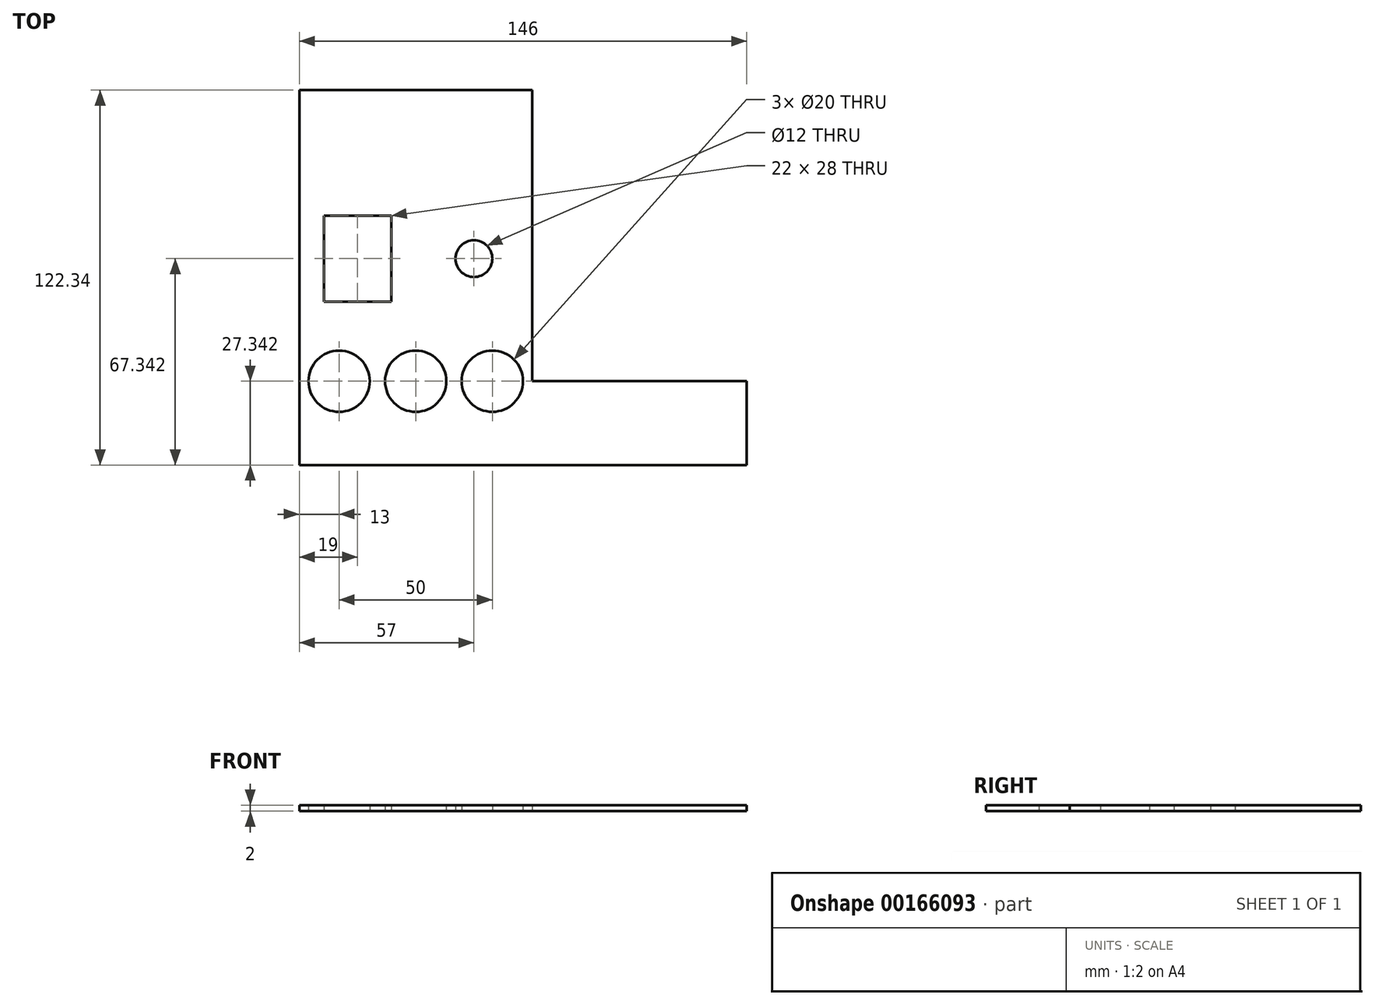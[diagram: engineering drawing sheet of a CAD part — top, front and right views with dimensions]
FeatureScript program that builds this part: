
annotation { "Feature Type Name" : "Feature", "Feature Type Description" : "" }
export const myFeature = defineFeature(function(context is Context, id is Id, definition is map)
    precondition{}
    {
        {
            var Q0;
            Q0=qCreatedBy(makeId("Top.planeOp"),FACE);
            var sketch = newSketch(context, id + "F0", { "sketchPlane" : qUnion([Q0])});
            skLineSegment(sketch, "E0.0", {"start": v(146, 0) * mm, "end": v(0, 0) * mm});
            skLineSegment(sketch, "E0.1", {"start": v(76, 122.34) * mm, "end": v(38, 122.34) * mm});
            skLineSegment(sketch, "E0.2", {"start": v(76, 122.34) * mm, "end": v(76, 27.34) * mm});
            skLineSegment(sketch, "E0.3", {"start": v(0, 0) * mm, "end": v(0, 122.34) * mm});
            skLineSegment(sketch, "E0.4", {"start": v(76, 27.34) * mm, "end": v(146, 27.34) * mm});
            skLineSegment(sketch, "E0.5", {"start": v(146, 0) * mm, "end": v(146, 27.34) * mm});
            skLineSegment(sketch, "E1", {"start": v(76, 27.34) * mm, "end": v(0, 27.34) * mm, "construction": true});
            skLineSegment(sketch, "E2", {"start": v(13, 46.21) * mm, "end": v(13, -10) * mm, "construction": true});
            skLineSegment(sketch, "E3", {"start": v(63, 46.64) * mm, "end": v(63, -8.92) * mm, "construction": true});
            skCircle(sketch, "E4", {"center": v(13, 27.34) * mm, "radius": 10 * mm});
            skCircle(sketch, "E5", {"center": v(38, 27.34) * mm, "radius": 10 * mm});
            skCircle(sketch, "E6", {"center": v(63, 27.34) * mm, "radius": 10 * mm});
            skLineSegment(sketch, "E7", {"start": v(38, 122.34) * mm, "end": v(38, -5.17) * mm, "construction": true});
            skLineSegment(sketch, "E8", {"start": v(38, 122.34) * mm, "end": v(0, 122.34) * mm});
            skLineSegment(sketch, "E9", {"start": v(93.77, 67.34) * mm, "end": v(-26.66, 67.34) * mm, "construction": true});
            skLineSegment(sketch, "E10.bottom", {"start": v(30, 53.34) * mm, "end": v(8, 53.34) * mm});
            skLineSegment(sketch, "E10.top", {"start": v(30, 81.34) * mm, "end": v(8, 81.34) * mm});
            skLineSegment(sketch, "E10.left", {"start": v(30, 53.34) * mm, "end": v(30, 81.34) * mm});
            skLineSegment(sketch, "E10.right", {"start": v(8, 53.34) * mm, "end": v(8, 81.34) * mm});
            skPoint(sketch, "E10.middle", {"position": v(19, 67.34) * mm});
            skCircle(sketch, "E11", {"center": v(57, 67.34) * mm, "radius": 6 * mm});
            skSolve(sketch);
        }
        {
            var Q0;
            Q0=makeQuery(id+"F0.imprint","IMPRINT",FACE,{"disambiguationData":[TD([[makeQuery(id+"F0.imprint","IMPRINT",EDGE,{"derivedFrom":sQuery(id+"F0.wireOp",EDGE,"E0.0")}),-1.0]])]});
            extrude(context, id + "F1", {"entities" : qUnion([Q0]), "depth" : 2 * mm});
        }
    });
